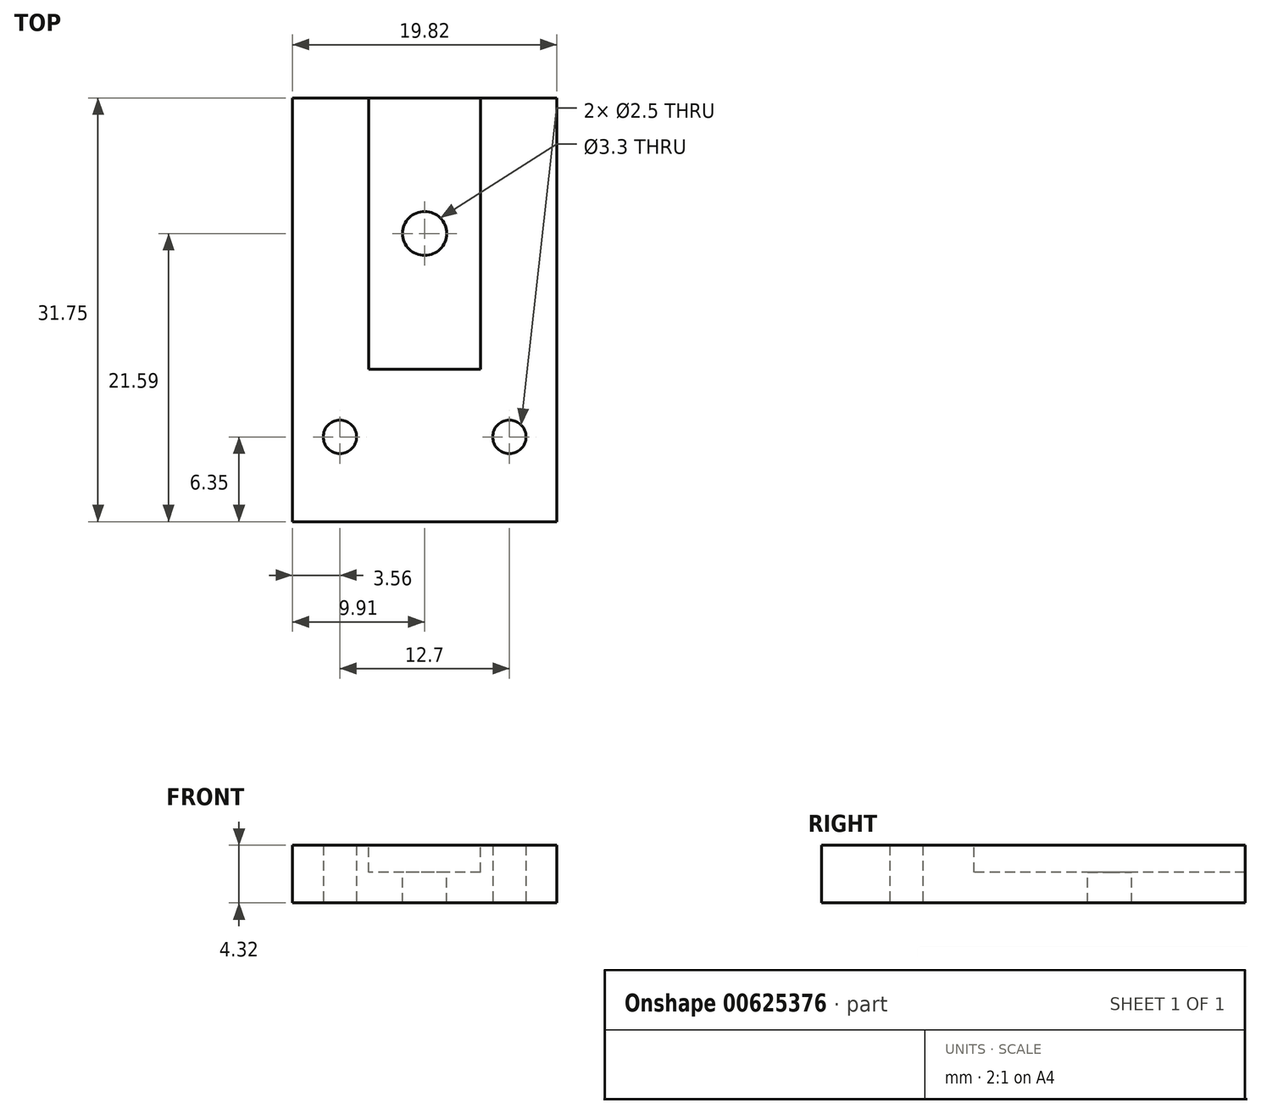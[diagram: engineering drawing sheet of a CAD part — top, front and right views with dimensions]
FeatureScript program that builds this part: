
annotation { "Feature Type Name" : "Feature", "Feature Type Description" : "" }
export const myFeature = defineFeature(function(context is Context, id is Id, definition is map)
    precondition{}
    {
        {
            var Q0;
            Q0=qCreatedBy(makeId("Top.planeOp"),FACE);
            var sketch = newSketch(context, id + "F0", { "sketchPlane" : qUnion([Q0])});
            skCircle(sketch, "E0", {"center": v(-6.35, 0) * mm, "radius": 1.25 * mm});
            skLineSegment(sketch, "E1", {"start": v(-9.9, 25.4) * mm, "end": v(-9.9, -6.35) * mm});
            skLineSegment(sketch, "E2", {"start": v(-9.9, -6.35) * mm, "end": v(9.9, -6.35) * mm});
            skLineSegment(sketch, "E3", {"start": v(9.9, -6.35) * mm, "end": v(9.9, 25.4) * mm});
            skLineSegment(sketch, "E4", {"start": v(9.9, 25.4) * mm, "end": v(-9.9, 25.4) * mm});
            skLineSegment(sketch, "E5", {"start": v(0, 0) * mm, "end": v(0, -6.35) * mm, "construction": true});
            skCircle(sketch, "E6.MirrorC", {"center": v(6.35, 0) * mm, "radius": 1.25 * mm});
            skSolve(sketch);
        }
        {
            var Q0;
            Q0 = qSketchRegion(id + "F0", true);
            extrude(context, id + "F1", {"entities" : qUnion([Q0]), "endBound" : BoundingType.SYMMETRIC, "depth" : 4.32 * mm, "offsetDistance" : 25.4 * mm});
        }
        {
            var Q0;
            Q0=makeQuery(id+"F1.opExtrude","CAP_FACE",FACE,{"disambiguationData":[OSD([sQuery(id+"F0.wireOp",EDGE,"E0"),sQuery(id+"F0.wireOp",EDGE,"E1"),sQuery(id+"F0.wireOp",EDGE,"E2"),sQuery(id+"F0.wireOp",EDGE,"E3"),sQuery(id+"F0.wireOp",EDGE,"E4"),sQuery(id+"F0.wireOp",EDGE,"E6.MirrorC")])],"isStart":false});
            var sketch = newSketch(context, id + "F2", { "sketchPlane" : qUnion([Q0])});
            skPoint(sketch, "E7", {"position": v(0, 15.24) * mm});
            skSolve(sketch);
        }
        {
            var Q0;
            Q0=sQuery(id+"F2.wireOp",VERTEX,"E7");
            var Q1;
            Q1=makeQuery(id+"F1.opExtrude","SWEPT_BODY",BODY,{"disambiguationData":[OSD([sQuery(id+"F0.wireOp",EDGE,"E0"),sQuery(id+"F0.wireOp",EDGE,"E1"),sQuery(id+"F0.wireOp",EDGE,"E2"),sQuery(id+"F0.wireOp",EDGE,"E3"),sQuery(id+"F0.wireOp",EDGE,"E4"),sQuery(id+"F0.wireOp",EDGE,"E6.MirrorC")])]});
            hole(context, id + "F3", {"style" : HoleStyle.SIMPLE, "endStyle" : HoleEndStyle.THROUGH, "standardTappedOrClearance" : lookupTablePath({ "standard" : "ISO", "engagement" : "75%", "pitch" : "0.7 mm", "size" : "M4", "type" : "Tapped" }), "standardBlindInLast" : lookupTablePath({ "standard" : "ISO", "engagement" : "75%", "pitch" : "0.7 mm", "size" : "M4", "type" : "Tapped" }), "holeDiameter" : 3.3 * mm, "majorDiameter" : 4 * mm, "showTappedDepth" : true, "isTappedThrough" : true, "tappedDepth" : 12.7 * mm, "tapClearance" : 3, "startFromSketch" : true, "locations" : qUnion([Q0]), "scope" : qUnion([Q1])});
        }
        {
            var Q0;
            Q0=makeQuery(id+"F1.opExtrude","CAP_FACE",FACE,{"disambiguationData":[OSD([sQuery(id+"F0.wireOp",EDGE,"E0"),sQuery(id+"F0.wireOp",EDGE,"E1"),sQuery(id+"F0.wireOp",EDGE,"E2"),sQuery(id+"F0.wireOp",EDGE,"E3"),sQuery(id+"F0.wireOp",EDGE,"E4"),sQuery(id+"F0.wireOp",EDGE,"E6.MirrorC")])],"isStart":false});
            var sketch = newSketch(context, id + "F4", { "sketchPlane" : qUnion([Q0])});
            skLineSegment(sketch, "E8", {"start": v(-4.2, 25.4) * mm, "end": v(-4.2, 5.08) * mm});
            skLineSegment(sketch, "E9", {"start": v(-4.2, 5.08) * mm, "end": v(4.2, 5.08) * mm});
            skLineSegment(sketch, "E10", {"start": v(4.2, 5.08) * mm, "end": v(4.2, 25.4) * mm});
            skLineSegment(sketch, "E11", {"start": v(4.2, 25.4) * mm, "end": v(-4.2, 25.4) * mm});
            skLineSegment(sketch, "E12", {"start": v(0, 0) * mm, "end": v(0, 5.08) * mm, "construction": true});
            skSolve(sketch);
        }
        {
            var Q0;
            Q0 = qSketchRegion(id + "F4", true);
            extrude(context, id + "F5", {"entities" : qUnion([Q0]), "operationType" : NewBodyOperationType.REMOVE, "oppositeDirection" : true, "depth" : 2.03 * mm, "offsetDistance" : 25.4 * mm});
        }
    });
